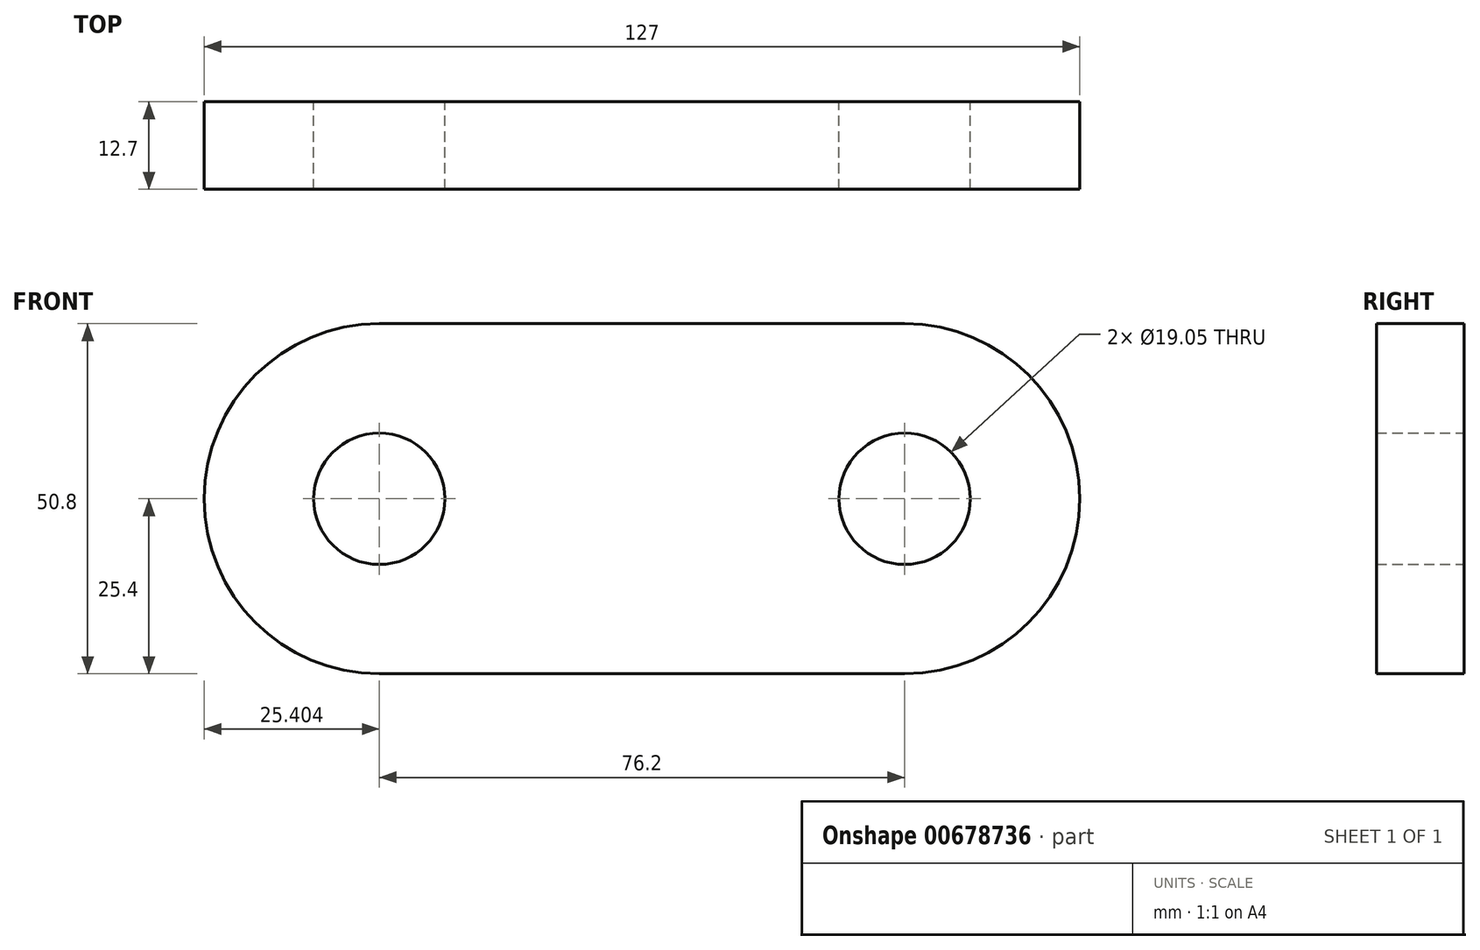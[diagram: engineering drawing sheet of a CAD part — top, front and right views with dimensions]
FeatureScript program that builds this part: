
annotation { "Feature Type Name" : "Feature", "Feature Type Description" : "" }
export const myFeature = defineFeature(function(context is Context, id is Id, definition is map)
    precondition{}
    {
        {
            var Q0;
            Q0=qCreatedBy(makeId("Front.planeOp"),FACE);
            var sketch = newSketch(context, id + "F0", { "sketchPlane" : qUnion([Q0])});
            skLineSegment(sketch, "E0", {"start": v(-39.09, 0) * mm, "end": v(37.11, 0) * mm});
            skArc(sketch, "E1", {"start": v(37.11, 0) * mm, "mid": v(62.51, 25.4) * mm, "end": v(37.11, 50.8) * mm});
            skArc(sketch, "E2", {"start": v(-39.09, 50.8) * mm, "mid": v(-64.49, 25.4) * mm, "end": v(-39.09, 0) * mm});
            skLineSegment(sketch, "E3", {"start": v(-39.09, 50.8) * mm, "end": v(37.11, 50.8) * mm});
            skCircle(sketch, "E4", {"center": v(-39.09, 25.4) * mm, "radius": 9.53 * mm});
            skCircle(sketch, "E5", {"center": v(37.11, 25.4) * mm, "radius": 9.53 * mm});
            skSolve(sketch);
        }
        {
            var Q0;
            Q0=makeQuery(id+"F0.imprint","IMPRINT",FACE,{"disambiguationData":[TD([[makeQuery(id+"F0.imprint","IMPRINT",EDGE,{"derivedFrom":sQuery(id+"F0.wireOp",EDGE,"E0")}),1.0]])]});
            extrude(context, id + "F1", {"entities" : qUnion([Q0]), "depth" : 12.7 * mm, "offsetDistance" : 25.4 * mm});
        }
    });
